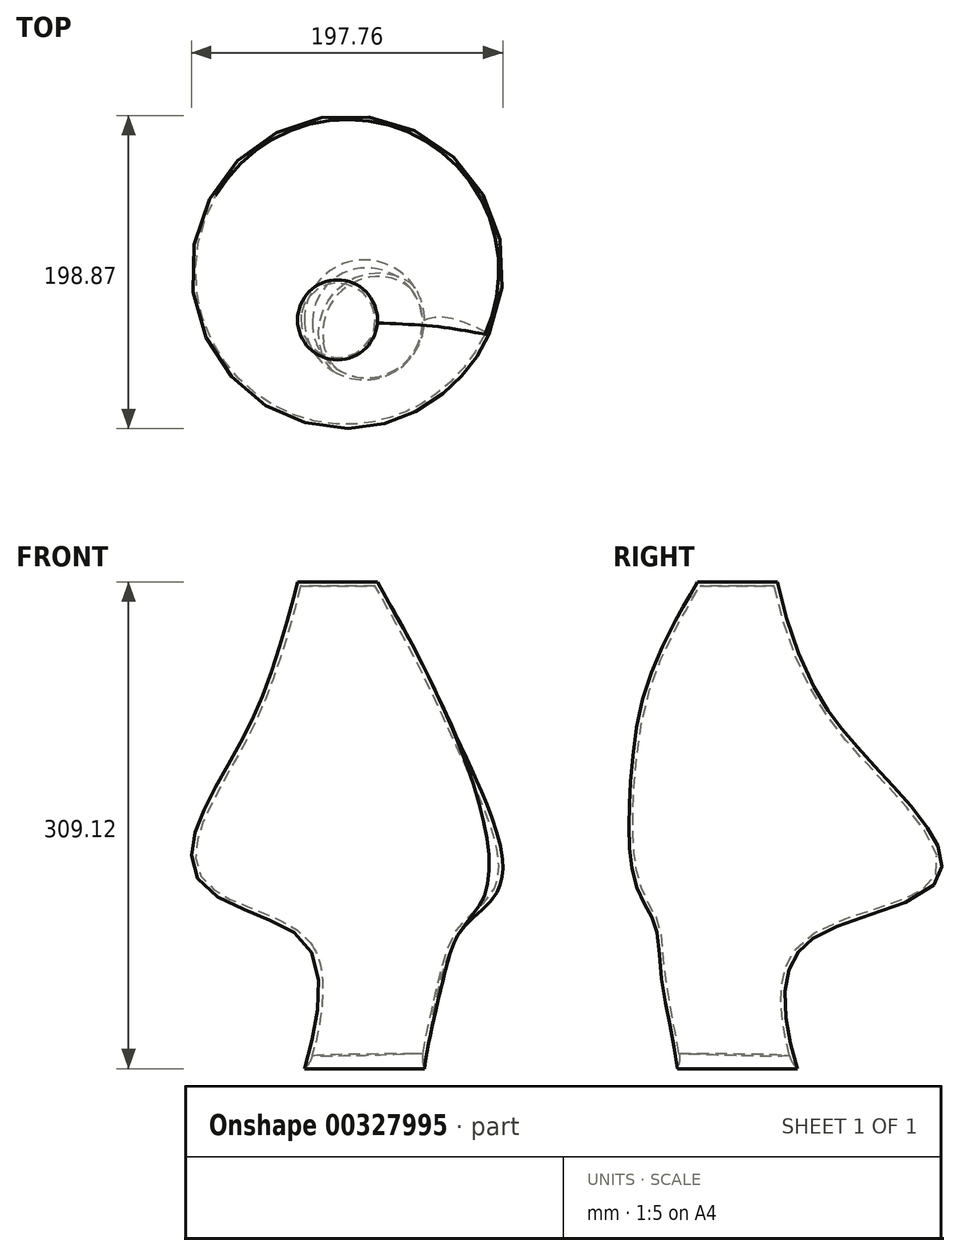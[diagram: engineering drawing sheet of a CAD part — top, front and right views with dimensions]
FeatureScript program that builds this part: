
annotation { "Feature Type Name" : "Feature", "Feature Type Description" : "" }
export const myFeature = defineFeature(function(context is Context, id is Id, definition is map)
    precondition{}
    {
        {
            var Q0;
            Q0=qCreatedBy(makeId("Top.planeOp"),FACE);
            cPlane(context, id + "F0", {"entities" : qUnion([Q0]), "cplaneType" : CPlaneType.OFFSET, "offset" : 84.58 * mm, "width" : 152.4 * mm, "height" : 152.4 * mm});
        }
        {
            var Q0;
            Q0=qCreatedBy(id+"F0.planeOp",FACE);
            cPlane(context, id + "F1", {"entities" : qUnion([Q0]), "cplaneType" : CPlaneType.OFFSET, "offset" : 25.4 * mm, "width" : 152.4 * mm, "height" : 152.4 * mm});
        }
        {
            var Q0;
            Q0=qCreatedBy(id+"F1.planeOp",FACE);
            cPlane(context, id + "F2", {"entities" : qUnion([Q0]), "cplaneType" : CPlaneType.OFFSET, "offset" : 109.47 * mm, "width" : 152.4 * mm, "height" : 152.4 * mm});
        }
        {
            var Q0;
            Q0=qCreatedBy(id+"F1.planeOp",FACE);
            cPlane(context, id + "F3", {"entities" : qUnion([Q0]), "cplaneType" : CPlaneType.OFFSET, "offset" : 199.14 * mm, "width" : 152.4 * mm, "height" : 152.4 * mm});
        }
        {
            var Q0;
            Q0=qCreatedBy(makeId("Top.planeOp"),FACE);
            var sketch = newSketch(context, id + "F4", { "sketchPlane" : qUnion([Q0])});
            skCircle(sketch, "E0", {"center": v(0, 0) * mm, "radius": 38.1 * mm});
            skSolve(sketch);
        }
        {
            var Q0;
            Q0=qCreatedBy(id+"F0.planeOp",FACE);
            var sketch = newSketch(context, id + "F5", { "sketchPlane" : qUnion([Q0])});
            skCircle(sketch, "E1", {"center": v(8.47, 0) * mm, "radius": 50.8 * mm});
            skSolve(sketch);
        }
        {
            var Q0;
            Q0=qCreatedBy(id+"F1.planeOp",FACE);
            var sketch = newSketch(context, id + "F6", { "sketchPlane" : qUnion([Q0])});
            skCircle(sketch, "E2", {"center": v(-5.87, 27.14) * mm, "radius": 88.9 * mm});
            skSolve(sketch);
        }
        {
            var Q0;
            Q0=qCreatedBy(id+"F2.planeOp",FACE);
            var sketch = newSketch(context, id + "F7", { "sketchPlane" : qUnion([Q0])});
            skCircle(sketch, "E3", {"center": v(-8.89, 0) * mm, "radius": 63.5 * mm});
            skSolve(sketch);
        }
        {
            var Q0;
            Q0=qCreatedBy(id+"F3.planeOp",FACE);
            var sketch = newSketch(context, id + "F8", { "sketchPlane" : qUnion([Q0])});
            skCircle(sketch, "E4", {"center": v(-17.1, 0) * mm, "radius": 25.4 * mm});
            skSolve(sketch);
        }
        {
            var Q0;
            Q0=makeQuery(id+"F4.imprint","IMPRINT",FACE,{"disambiguationData":[TD([[makeQuery(id+"F4.imprint","IMPRINT",EDGE,{"derivedFrom":sQuery(id+"F4.wireOp",EDGE,"E0")}),1.0]])]});
            var Q1;
            Q1=makeQuery(id+"F5.imprint","IMPRINT",FACE,{"disambiguationData":[TD([[makeQuery(id+"F5.imprint","IMPRINT",EDGE,{"derivedFrom":sQuery(id+"F5.wireOp",EDGE,"E1")}),1.0]])]});
            var Q2;
            Q2=makeQuery(id+"F6.imprint","IMPRINT",FACE,{"disambiguationData":[TD([[makeQuery(id+"F6.imprint","IMPRINT",EDGE,{"derivedFrom":sQuery(id+"F6.wireOp",EDGE,"E2")}),1.0]])]});
            var Q3;
            Q3=makeQuery(id+"F7.imprint","IMPRINT",FACE,{"disambiguationData":[TD([[makeQuery(id+"F7.imprint","IMPRINT",EDGE,{"derivedFrom":sQuery(id+"F7.wireOp",EDGE,"E3")}),1.0]])]});
            var Q4;
            Q4=makeQuery(id+"F8.imprint","IMPRINT",FACE,{"disambiguationData":[TD([[makeQuery(id+"F8.imprint","IMPRINT",EDGE,{"derivedFrom":sQuery(id+"F8.wireOp",EDGE,"E4")}),1.0]])]});
            loft(context, id + "F9", {"sheetProfilesArray" : [{ "sheetProfileEntities" : qUnion([Q0]) }, { "sheetProfileEntities" : qUnion([Q1]) }, { "sheetProfileEntities" : qUnion([Q2]) }, { "sheetProfileEntities" : qUnion([Q3]) }, { "sheetProfileEntities" : qUnion([Q4]) }]});
        }
        {
            var Q0;
            Q0=makeQuery(id+"F9.opLoft","CAP_FACE",FACE,{"disambiguationData":[OSD([makeQuery(id+"F4.imprint","IMPRINT",FACE,{"disambiguationData":[TD([[makeQuery(id+"F4.imprint","IMPRINT",EDGE,{"derivedFrom":sQuery(id+"F4.wireOp",EDGE,"E0")}),1.0]])]})])],"isStart":true});
            shell(context, id + "F10", {"entities" : qUnion([Q0]), "thickness" : 2.54 * mm});
        }
        {
            var Q0;
            Q0=qCreatedBy(id+"F1.planeOp",FACE);
            var sketch = newSketch(context, id + "F11", { "sketchPlane" : qUnion([Q0])});
            skCircle(sketch, "E5", {"center": v(-42.04, 59.87) * mm, "radius": 25.4 * mm});
            skSolve(sketch);
        }
        {
            var Q0;
            Q0=sQuery(id+"F11.wireOp",EDGE,"E5");
            extrude(context, id + "F12", {"bodyType" : ToolBodyType.SURFACE, "surfaceEntities" : qUnion([Q0]), "oppositeDirection" : true, "depth" : 31.5 * mm});
        }
        {
            var Q0;
            Q0=makeQuery(id+"F10.opShell","OFFSET_EDGE",EDGE,{"disambiguationData":[OSD([sQuery(id+"F4.wireOp",EDGE,"E0")])]});
            fillet(context, id + "F13", {"entities" : qUnion([Q0]), "radius" : 17.78 * mm, "tangentPropagation" : true, "allowEdgeOverflow" : false});
        }
    });
